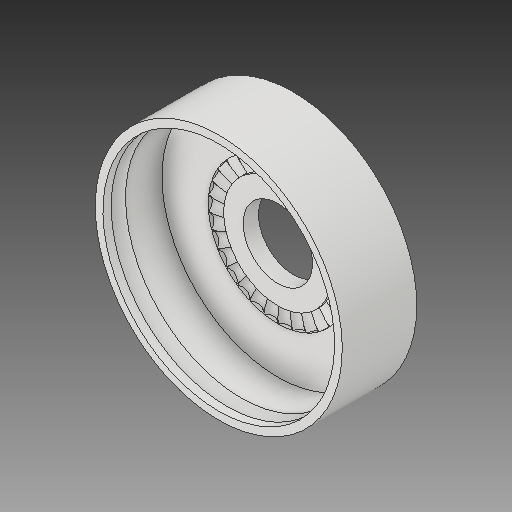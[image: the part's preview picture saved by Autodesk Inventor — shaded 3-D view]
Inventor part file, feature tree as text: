
AUTODESK INVENTOR PART (.ipt)
format: ipt  version: 2018 (Build 220112000, 112)  size: 346,624 bytes
history: native  units: in
note: dims shown in document units (in); Inventor stores cm internally (conversion verified against a paired STEP export)
features: sketch x5, extrude x4, projected_geometry x2, pattern_circular x1, revolve x1
ambient origin geometry x8: Origin, YZ Plane, XZ Plane, XY Plane, X Axis, Y Axis, Z Axis, Center Point
bodies: Solid1 (feature_tree)
feature tree (13):
  extrude  "Extrusion1"  Depth=0.125in TaperAngle=0.0deg
  extrude  "Extrusion2"  Depth=1.75in
  extrude  "Extrusion3"  Depth=0.125in TaperAngle=0.0deg
  pattern_circular  "Circular Pattern1"  [2 undecoded]
  extrude  "Extrusion4"  Depth=1.875in TaperAngle=360.0deg
  revolve  "Revolution1"  [1 undecoded]
  sketch  "Sketch1"  dims[d0=3.998in d1=0.125in d2=0.0in]
  sketch  "Sketch3"  dims[d3=0.375in d4=1.75in]
  sketch  "Sketch4"  dims[d6=0.25in d7=0.125in d8=0.0in]
  sketch  "Sketch5"  dims[d9=0.125in]
  projected_geometry  "Projected Loop1"
  sketch  "Sketch6"  dims[d10=0.0625in d11=1.25in d12=0.0in d13=11.811in d14=360.0deg d16=0.125in d17=1.75in d18=2.25in d19=0.125in d20=1.25in d21=0.0in d22=1.125in d23=0.135in d24=0.706in d26=1.875in d27=0.956in d29=0.0675in d30=0.0675in d31=1.875in d32=90.0deg]
  projected_geometry  "Projected Loop2"
note: 3 required parameter values undecoded (feature->parameter linkage not recoverable at this tier; creation-order binding heuristic only, values carry confidence <= 0.55)